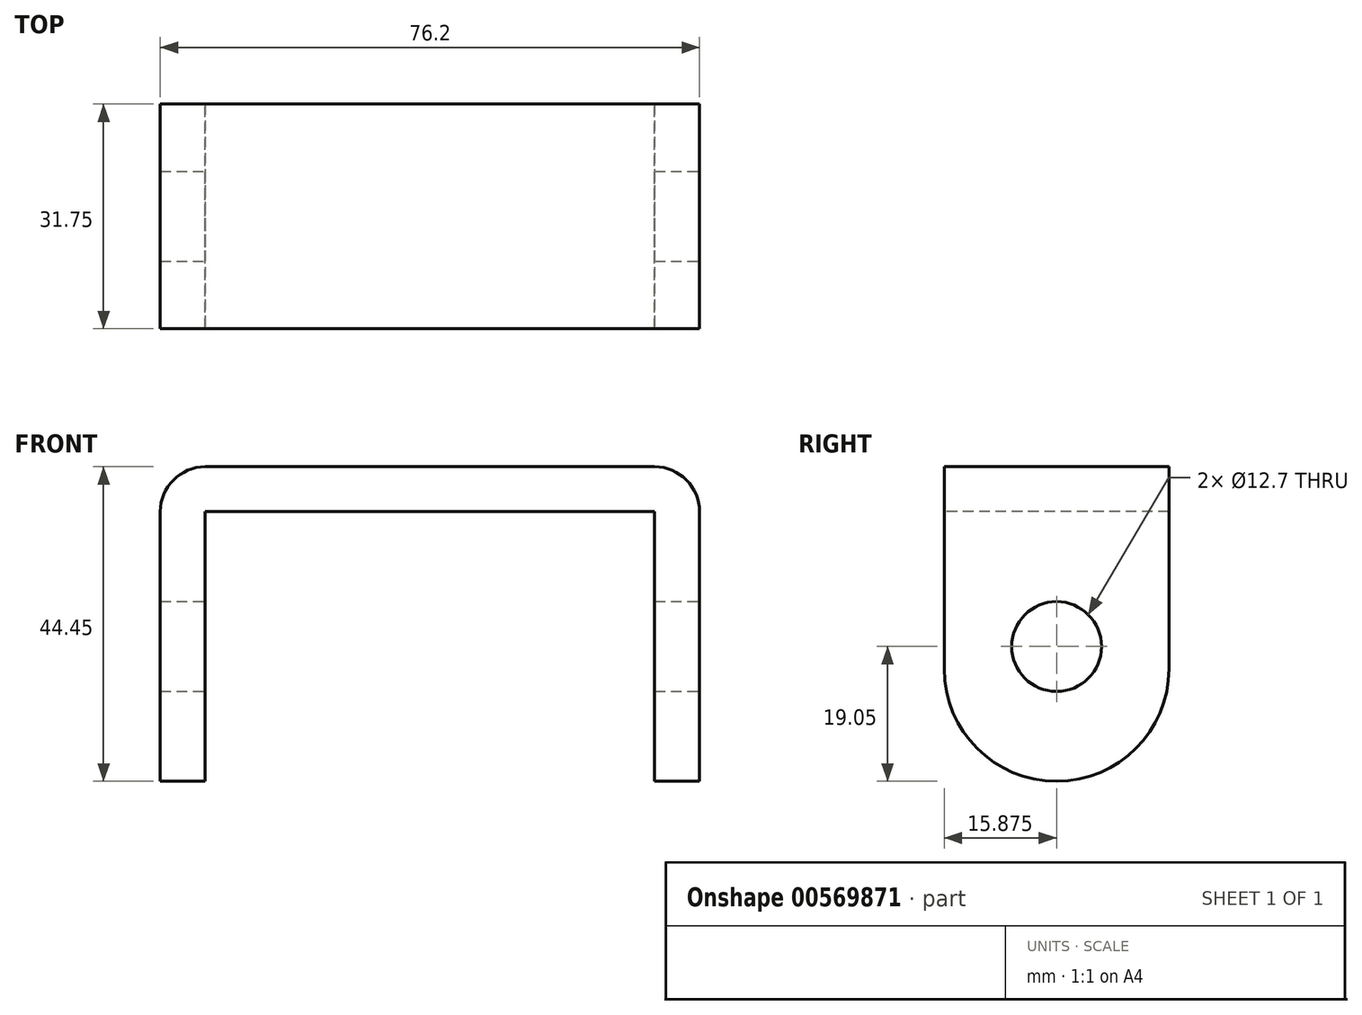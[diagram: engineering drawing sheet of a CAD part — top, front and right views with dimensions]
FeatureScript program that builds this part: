
annotation { "Feature Type Name" : "Feature", "Feature Type Description" : "" }
export const myFeature = defineFeature(function(context is Context, id is Id, definition is map)
    precondition{}
    {
        {
            var Q0;
            Q0=qCreatedBy(makeId("Front.planeOp"),FACE);
            var sketch = newSketch(context, id + "F0", { "sketchPlane" : qUnion([Q0])});
            skLineSegment(sketch, "E0.bottom", {"start": v(0, 0) * mm, "end": v(-76.2, 0) * mm});
            skLineSegment(sketch, "E0.top", {"start": v(0, 6.35) * mm, "end": v(-76.2, 6.35) * mm});
            skLineSegment(sketch, "E0.left", {"start": v(0, 0) * mm, "end": v(0, 6.35) * mm});
            skLineSegment(sketch, "E0.right", {"start": v(-76.2, 0) * mm, "end": v(-76.2, 6.35) * mm});
            skLineSegment(sketch, "E1.bottom", {"start": v(-76.2, 0) * mm, "end": v(-69.85, 0) * mm});
            skLineSegment(sketch, "E1.top", {"start": v(-76.2, -38.1) * mm, "end": v(-69.85, -38.1) * mm});
            skLineSegment(sketch, "E1.left", {"start": v(-76.2, 0) * mm, "end": v(-76.2, -38.1) * mm});
            skLineSegment(sketch, "E1.right", {"start": v(-69.85, 0) * mm, "end": v(-69.85, -38.1) * mm});
            skLineSegment(sketch, "E2.bottom", {"start": v(0, 0) * mm, "end": v(-6.35, 0) * mm});
            skLineSegment(sketch, "E2.top", {"start": v(0, -38.1) * mm, "end": v(-6.35, -38.1) * mm});
            skLineSegment(sketch, "E2.left", {"start": v(0, 0) * mm, "end": v(0, -38.1) * mm});
            skLineSegment(sketch, "E2.right", {"start": v(-6.35, 0) * mm, "end": v(-6.35, -38.1) * mm});
            skSolve(sketch);
        }
        {
            var Q0;
            Q0 = qSketchRegion(id + "F0", true);
            extrude(context, id + "F1", {"entities" : qUnion([Q0]), "depth" : 31.75 * mm, "offsetDistance" : 25.4 * mm});
        }
        {
            var Q0;
            Q0=makeQuery(id+"F1.opExtrude","SWEPT_FACE",FACE,{"disambiguationData":[OSD([sQuery(id+"F0.wireOp",EDGE,"E0.left"),sQuery(id+"F0.wireOp",EDGE,"E2.left")])]});
            var sketch = newSketch(context, id + "F2", { "sketchPlane" : qUnion([Q0])});
            skCircle(sketch, "E3", {"center": v(-15.88, -19.05) * mm, "radius": 6.35 * mm});
            skSolve(sketch);
        }
        {
            var Q0;
            Q0 = qSketchRegion(id + "F2", true);
            extrude(context, id + "F3", {"entities" : qUnion([Q0]), "operationType" : NewBodyOperationType.REMOVE, "oppositeDirection" : true, "depth" : 127 * mm, "offsetDistance" : 25.4 * mm});
        }
        {
            var Q0;
            Q0=makeQuery(id+"F1.opExtrude","SWEPT_FACE",FACE,{"disambiguationData":[OSD([sQuery(id+"F0.wireOp",EDGE,"E0.left"),sQuery(id+"F0.wireOp",EDGE,"E2.left")])]});
            var sketch = newSketch(context, id + "F4", { "sketchPlane" : qUnion([Q0])});
            skLineSegment(sketch, "E4.bottom", {"start": v(-15.88, -38.1) * mm, "end": v(-15.87, -38.1) * mm});
            skLineSegment(sketch, "E4.top", {"start": v(-31.75, 6.35) * mm, "end": v(0, 6.35) * mm});
            skLineSegment(sketch, "E4.left", {"start": v(-31.75, -22.23) * mm, "end": v(-31.75, 6.35) * mm});
            skLineSegment(sketch, "E4.right", {"start": v(0, -22.22) * mm, "end": v(0, 6.35) * mm});
            skPoint(sketch, "E5.visualSharp", {"position": v(-31.75, -38.1) * mm});
            skArc(sketch, "E5.filletArc", {"start": v(-31.75, -22.23) * mm, "mid": v(-27.1, -33.45) * mm, "end": v(-15.88, -38.1) * mm});
            skPoint(sketch, "E6.visualSharp", {"position": v(0, -38.1) * mm});
            skArc(sketch, "E6.filletArc", {"start": v(-15.87, -38.1) * mm, "mid": v(-4.65, -33.45) * mm, "end": v(0, -22.22) * mm});
            skSolve(sketch);
        }
        {
            var Q0;
            {var subQ0=sQuery(id+"F4.wireOp",EDGE,"E5.filletArc");Q0=makeQuery(id+"F4.imprint","IMPRINT",FACE,{"disambiguationData":[TD([[makeQuery(id+"F4.imprint","IMPRINT",EDGE,{"derivedFrom":subQ0}),-1.0]])]});}
            var Q1;
            {var subQ0=sQuery(id+"F4.wireOp",EDGE,"E6.filletArc");Q1=makeQuery(id+"F4.imprint","IMPRINT",FACE,{"disambiguationData":[TD([[makeQuery(id+"F4.imprint","IMPRINT",EDGE,{"derivedFrom":subQ0}),-1.0]])]});}
            extrude(context, id + "F5", {"entities" : qUnion([Q0, Q1]), "operationType" : NewBodyOperationType.REMOVE, "oppositeDirection" : true, "depth" : 127 * mm, "offsetDistance" : 25.4 * mm});
        }
        {
            var Q0;
            Q0=makeQuery(id+"F1.opExtrude","CAP_FACE",FACE,{"disambiguationData":[OSD([sQuery(id+"F0.wireOp",EDGE,"E0.bottom"),sQuery(id+"F0.wireOp",EDGE,"E0.top"),sQuery(id+"F0.wireOp",EDGE,"E0.left"),sQuery(id+"F0.wireOp",EDGE,"E0.right"),sQuery(id+"F0.wireOp",EDGE,"E1.top"),sQuery(id+"F0.wireOp",EDGE,"E1.left"),sQuery(id+"F0.wireOp",EDGE,"E1.right"),sQuery(id+"F0.wireOp",EDGE,"E2.top"),sQuery(id+"F0.wireOp",EDGE,"E2.left"),sQuery(id+"F0.wireOp",EDGE,"E2.right")])],"isStart":false});
            var sketch = newSketch(context, id + "F6", { "sketchPlane" : qUnion([Q0])});
            skLineSegment(sketch, "E7.bottom", {"start": v(-69.85, 6.35) * mm, "end": v(-6.35, 6.35) * mm});
            skLineSegment(sketch, "E7.top", {"start": v(-63.5, 0) * mm, "end": v(-12.7, 0) * mm});
            skLineSegment(sketch, "E7.left", {"start": v(-76.2, 0) * mm, "end": v(-76.2, 0) * mm});
            skLineSegment(sketch, "E7.right", {"start": v(0, 0) * mm, "end": v(0, 0) * mm});
            skLineSegment(sketch, "E8.bottom", {"start": v(0, 0) * mm, "end": v(-6.35, 0) * mm});
            skLineSegment(sketch, "E8.top", {"start": v(0, -22.23) * mm, "end": v(-6.35, -22.23) * mm});
            skLineSegment(sketch, "E8.left", {"start": v(0, 0) * mm, "end": v(0, -22.23) * mm});
            skLineSegment(sketch, "E8.right", {"start": v(-6.35, -6.35) * mm, "end": v(-6.35, -22.23) * mm});
            skLineSegment(sketch, "E9.bottom", {"start": v(-69.85, -22.23) * mm, "end": v(-76.2, -22.23) * mm});
            skLineSegment(sketch, "E9.top", {"start": v(-69.85, 0) * mm, "end": v(-76.2, 0) * mm});
            skLineSegment(sketch, "E9.left", {"start": v(-69.85, -22.23) * mm, "end": v(-69.85, -6.35) * mm});
            skLineSegment(sketch, "E9.right", {"start": v(-76.2, -22.23) * mm, "end": v(-76.2, 0) * mm});
            skPoint(sketch, "E10.visualSharp", {"position": v(-76.2, 6.35) * mm});
            skArc(sketch, "E10.filletArc", {"start": v(-69.85, 6.35) * mm, "mid": v(-74.34, 4.5) * mm, "end": v(-76.2, 0) * mm});
            skArc(sketch, "E11.filletArc", {"start": v(-63.5, 0) * mm, "mid": v(-68, -1.86) * mm, "end": v(-69.85, -6.35) * mm});
            skArc(sketch, "E12.filletArc", {"start": v(-6.35, -6.35) * mm, "mid": v(-8.2, -1.86) * mm, "end": v(-12.7, 0) * mm});
            skPoint(sketch, "E13.visualSharp", {"position": v(0, 6.35) * mm});
            skArc(sketch, "E13.filletArc", {"start": v(0, 0) * mm, "mid": v(-1.86, 4.5) * mm, "end": v(-6.35, 6.35) * mm});
            skSolve(sketch);
        }
        {
            var Q0;
            {var subQ0=sQuery(id+"F6.wireOp",EDGE,"E11.filletArc");Q0=makeQuery(id+"F6.imprint","IMPRINT",FACE,{"disambiguationData":[TD([[makeQuery(id+"F6.imprint","IMPRINT",EDGE,{"derivedFrom":subQ0}),-1.0]])]});}
            var Q1;
            {var subQ0=sQuery(id+"F6.wireOp",EDGE,"E12.filletArc");Q1=makeQuery(id+"F6.imprint","IMPRINT",FACE,{"disambiguationData":[TD([[makeQuery(id+"F6.imprint","IMPRINT",EDGE,{"derivedFrom":subQ0}),-1.0]])]});}
            extrude(context, id + "F7", {"entities" : qUnion([Q0, Q1]), "operationType" : NewBodyOperationType.ADD, "oppositeDirection" : true, "depth" : 31.75 * mm, "offsetDistance" : 25.4 * mm});
        }
        {
            var Q0;
            {var subQ0=sQuery(id+"F6.wireOp",EDGE,"E10.filletArc");Q0=makeQuery(id+"F6.imprint","IMPRINT",FACE,{"disambiguationData":[TD([[makeQuery(id+"F6.imprint","IMPRINT",EDGE,{"derivedFrom":subQ0}),-1.0]])]});}
            var Q1;
            {var subQ0=sQuery(id+"F6.wireOp",EDGE,"E13.filletArc");Q1=makeQuery(id+"F6.imprint","IMPRINT",FACE,{"disambiguationData":[TD([[makeQuery(id+"F6.imprint","IMPRINT",EDGE,{"derivedFrom":subQ0}),-1.0]])]});}
            var Q2;
            {var subQ0=sQuery(id+"F6.wireOp",EDGE,"E11.filletArc");Q2=makeQuery(id+"F6.imprint","IMPRINT",FACE,{"disambiguationData":[TD([[makeQuery(id+"F6.imprint","IMPRINT",EDGE,{"derivedFrom":subQ0}),-1.0]])]});}
            var Q3;
            {var subQ0=sQuery(id+"F6.wireOp",EDGE,"E12.filletArc");Q3=makeQuery(id+"F6.imprint","IMPRINT",FACE,{"disambiguationData":[TD([[makeQuery(id+"F6.imprint","IMPRINT",EDGE,{"derivedFrom":subQ0}),-1.0]])]});}
            extrude(context, id + "F8", {"entities" : qUnion([Q0, Q1, Q2, Q3]), "operationType" : NewBodyOperationType.REMOVE, "oppositeDirection" : true, "depth" : 31.75 * mm, "offsetDistance" : 25.4 * mm});
        }
    });
